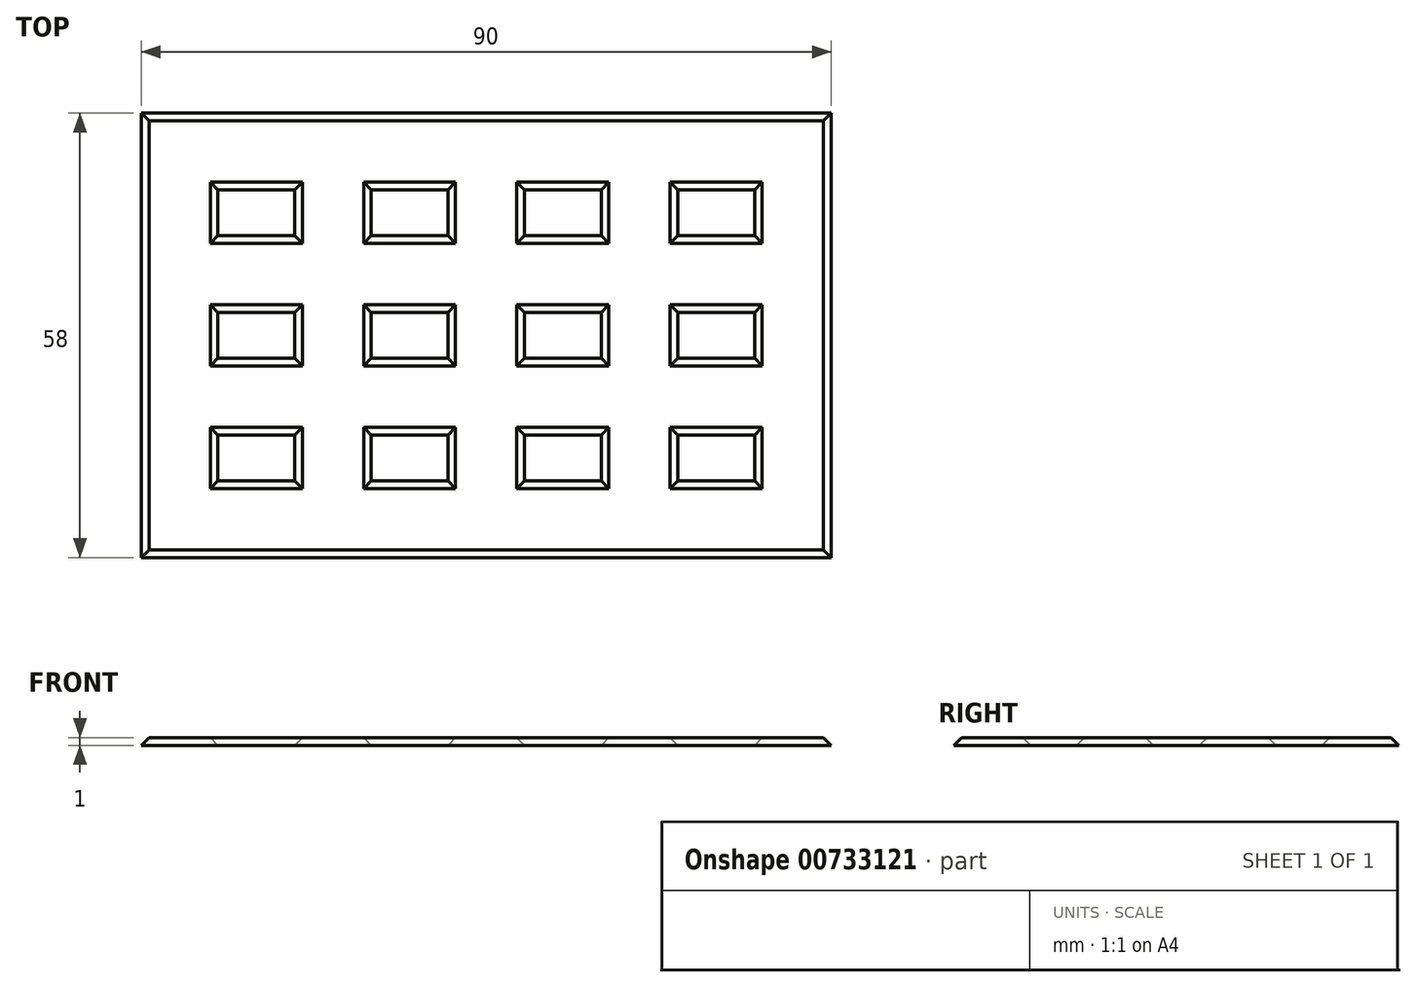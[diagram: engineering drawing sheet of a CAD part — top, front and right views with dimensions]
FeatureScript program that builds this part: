
annotation { "Feature Type Name" : "Feature", "Feature Type Description" : "" }
export const myFeature = defineFeature(function(context is Context, id is Id, definition is map)
    precondition{}
    {
        {
            var Q0;
            Q0=qCreatedBy(makeId("Top.planeOp"),FACE);
            var sketch = newSketch(context, id + "F0", { "sketchPlane" : qUnion([Q0])});
            skPoint(sketch, "E0.middle", {"position": v(0, 0) * mm});
            skLineSegment(sketch, "E1.bottom", {"start": v(-40, 15) * mm, "end": v(-30, 15) * mm});
            skLineSegment(sketch, "E1.top", {"start": v(-40, 9) * mm, "end": v(-30, 9) * mm});
            skLineSegment(sketch, "E1.left", {"start": v(-40, 15) * mm, "end": v(-40, 9) * mm});
            skLineSegment(sketch, "E1.right", {"start": v(-30, 15) * mm, "end": v(-30, 9) * mm});
            skLineSegment(sketch, "E2.bottom", {"start": v(-40, 9) * mm, "end": v(-30, 9) * mm, "construction": true});
            skLineSegment(sketch, "E2.top", {"start": v(-40, -1) * mm, "end": v(-30, -1) * mm, "construction": true});
            skLineSegment(sketch, "E2.left", {"start": v(-40, 9) * mm, "end": v(-40, -1) * mm, "construction": true});
            skLineSegment(sketch, "E2.right", {"start": v(-30, 9) * mm, "end": v(-30, -1) * mm, "construction": true});
            skLineSegment(sketch, "E3.bottom", {"start": v(-40, -1) * mm, "end": v(-30, -1) * mm});
            skLineSegment(sketch, "E3.top", {"start": v(-40, -7) * mm, "end": v(-30, -7) * mm});
            skLineSegment(sketch, "E3.left", {"start": v(-40, -1) * mm, "end": v(-40, -7) * mm});
            skLineSegment(sketch, "E3.right", {"start": v(-30, -1) * mm, "end": v(-30, -7) * mm});
            skLineSegment(sketch, "E4.bottom", {"start": v(-40, -7) * mm, "end": v(-30, -7) * mm, "construction": true});
            skLineSegment(sketch, "E4.top", {"start": v(-40, -17) * mm, "end": v(-30, -17) * mm, "construction": true});
            skLineSegment(sketch, "E4.left", {"start": v(-40, -7) * mm, "end": v(-40, -17) * mm, "construction": true});
            skLineSegment(sketch, "E4.right", {"start": v(-30, -7) * mm, "end": v(-30, -17) * mm, "construction": true});
            skLineSegment(sketch, "E5.bottom", {"start": v(-40, -17) * mm, "end": v(-30, -17) * mm});
            skLineSegment(sketch, "E5.top", {"start": v(-40, -23) * mm, "end": v(-30, -23) * mm});
            skLineSegment(sketch, "E5.left", {"start": v(-40, -17) * mm, "end": v(-40, -23) * mm});
            skLineSegment(sketch, "E5.right", {"start": v(-30, -17) * mm, "end": v(-30, -23) * mm});
            skLineSegment(sketch, "E6.bottom", {"start": v(-40, -23) * mm, "end": v(-30, -23) * mm, "construction": true});
            skLineSegment(sketch, "E6.top", {"start": v(-40, -33) * mm, "end": v(-30, -33) * mm, "construction": true});
            skLineSegment(sketch, "E6.left", {"start": v(-40, -23) * mm, "end": v(-40, -33) * mm, "construction": true});
            skLineSegment(sketch, "E6.right", {"start": v(-30, -23) * mm, "end": v(-30, -33) * mm, "construction": true});
            skLineSegment(sketch, "E7.bottom", {"start": v(-50, 25) * mm, "end": v(40, 25) * mm});
            skLineSegment(sketch, "E7.top", {"start": v(-50, -33) * mm, "end": v(40, -33) * mm});
            skLineSegment(sketch, "E7.left", {"start": v(-50, 25) * mm, "end": v(-50, -33) * mm});
            skLineSegment(sketch, "E7.right", {"start": v(40, 25) * mm, "end": v(40, -33) * mm});
            skLineSegment(sketch, "E8.bottom", {"start": v(-30, 15) * mm, "end": v(-20, 15) * mm, "construction": true});
            skLineSegment(sketch, "E8.top", {"start": v(-30, 9) * mm, "end": v(-20, 9) * mm, "construction": true});
            skLineSegment(sketch, "E8.left", {"start": v(-30, 15) * mm, "end": v(-30, 9) * mm, "construction": true});
            skLineSegment(sketch, "E8.right", {"start": v(-20, 15) * mm, "end": v(-20, 9) * mm, "construction": true});
            skLineSegment(sketch, "E9.bottom", {"start": v(-20, 9) * mm, "end": v(-30, 9) * mm, "construction": true});
            skLineSegment(sketch, "E9.top", {"start": v(-20, -1) * mm, "end": v(-30, -1) * mm, "construction": true});
            skLineSegment(sketch, "E9.left", {"start": v(-20, 9) * mm, "end": v(-20, -1) * mm, "construction": true});
            skLineSegment(sketch, "E10.top", {"start": v(-20, -7) * mm, "end": v(-30, -7) * mm, "construction": true});
            skLineSegment(sketch, "E10.left", {"start": v(-20, -1) * mm, "end": v(-20, -7) * mm, "construction": true});
            skLineSegment(sketch, "E10.right", {"start": v(-30, -1) * mm, "end": v(-30, -7) * mm, "construction": true});
            skLineSegment(sketch, "E11.top", {"start": v(-20, -17) * mm, "end": v(-30, -17) * mm, "construction": true});
            skLineSegment(sketch, "E11.left", {"start": v(-20, -7) * mm, "end": v(-20, -17) * mm, "construction": true});
            skLineSegment(sketch, "E12.top", {"start": v(-20, -23) * mm, "end": v(-30, -23) * mm, "construction": true});
            skLineSegment(sketch, "E12.left", {"start": v(-20, -17) * mm, "end": v(-20, -23) * mm, "construction": true});
            skLineSegment(sketch, "E12.right", {"start": v(-30, -17) * mm, "end": v(-30, -23) * mm, "construction": true});
            skLineSegment(sketch, "E13.bottom", {"start": v(-20, 15) * mm, "end": v(-10, 15) * mm});
            skLineSegment(sketch, "E13.top", {"start": v(-20, 9) * mm, "end": v(-10, 9) * mm});
            skLineSegment(sketch, "E13.left", {"start": v(-20, 15) * mm, "end": v(-20, 9) * mm});
            skLineSegment(sketch, "E13.right", {"start": v(-10, 15) * mm, "end": v(-10, 9) * mm});
            skLineSegment(sketch, "E14.bottom", {"start": v(-20, -1) * mm, "end": v(-10, -1) * mm});
            skLineSegment(sketch, "E14.top", {"start": v(-20, -7) * mm, "end": v(-10, -7) * mm});
            skLineSegment(sketch, "E14.left", {"start": v(-20, -1) * mm, "end": v(-20, -7) * mm});
            skLineSegment(sketch, "E14.right", {"start": v(-10, -1) * mm, "end": v(-10, -7) * mm});
            skLineSegment(sketch, "E15.bottom", {"start": v(-20, -17) * mm, "end": v(-10, -17) * mm});
            skLineSegment(sketch, "E15.top", {"start": v(-20, -23) * mm, "end": v(-10, -23) * mm});
            skLineSegment(sketch, "E15.left", {"start": v(-20, -17) * mm, "end": v(-20, -23) * mm});
            skLineSegment(sketch, "E15.right", {"start": v(-10, -17) * mm, "end": v(-10, -23) * mm});
            skLineSegment(sketch, "E16.bottom", {"start": v(-10, 15) * mm, "end": v(0, 15) * mm, "construction": true});
            skLineSegment(sketch, "E16.top", {"start": v(-10, 9) * mm, "end": v(0, 9) * mm, "construction": true});
            skLineSegment(sketch, "E16.left", {"start": v(-10, 15) * mm, "end": v(-10, 9) * mm, "construction": true});
            skLineSegment(sketch, "E16.right", {"start": v(0, 15) * mm, "end": v(0, 9) * mm, "construction": true});
            skLineSegment(sketch, "E17.bottom", {"start": v(-10, -1) * mm, "end": v(0, -1) * mm, "construction": true});
            skLineSegment(sketch, "E17.top", {"start": v(-10, -7) * mm, "end": v(0, -7) * mm, "construction": true});
            skLineSegment(sketch, "E17.left", {"start": v(-10, -1) * mm, "end": v(-10, -7) * mm, "construction": true});
            skLineSegment(sketch, "E17.right", {"start": v(0, -1) * mm, "end": v(0, -7) * mm, "construction": true});
            skLineSegment(sketch, "E18.bottom", {"start": v(-10, -17) * mm, "end": v(0, -17) * mm, "construction": true});
            skLineSegment(sketch, "E18.top", {"start": v(-10, -23) * mm, "end": v(0, -23) * mm, "construction": true});
            skLineSegment(sketch, "E18.left", {"start": v(-10, -17) * mm, "end": v(-10, -23) * mm, "construction": true});
            skLineSegment(sketch, "E18.right", {"start": v(0, -17) * mm, "end": v(0, -23) * mm, "construction": true});
            skLineSegment(sketch, "E19.bottom", {"start": v(0, 15) * mm, "end": v(10, 15) * mm});
            skLineSegment(sketch, "E19.top", {"start": v(0, 9) * mm, "end": v(10, 9) * mm});
            skLineSegment(sketch, "E19.left", {"start": v(0, 15) * mm, "end": v(0, 9) * mm});
            skLineSegment(sketch, "E19.right", {"start": v(10, 15) * mm, "end": v(10, 9) * mm});
            skLineSegment(sketch, "E20.bottom", {"start": v(0, -7) * mm, "end": v(10, -7) * mm});
            skLineSegment(sketch, "E20.top", {"start": v(0, -1) * mm, "end": v(10, -1) * mm});
            skLineSegment(sketch, "E20.left", {"start": v(0, -7) * mm, "end": v(0, -1) * mm});
            skLineSegment(sketch, "E20.right", {"start": v(10, -7) * mm, "end": v(10, -1) * mm});
            skLineSegment(sketch, "E21.bottom", {"start": v(0, -23) * mm, "end": v(10, -23) * mm});
            skLineSegment(sketch, "E21.top", {"start": v(0, -17) * mm, "end": v(10, -17) * mm});
            skLineSegment(sketch, "E21.left", {"start": v(0, -23) * mm, "end": v(0, -17) * mm});
            skLineSegment(sketch, "E21.right", {"start": v(10, -23) * mm, "end": v(10, -17) * mm});
            skLineSegment(sketch, "E22.bottom", {"start": v(10, 9) * mm, "end": v(20, 9) * mm, "construction": true});
            skLineSegment(sketch, "E22.top", {"start": v(10, 15) * mm, "end": v(20, 15) * mm, "construction": true});
            skLineSegment(sketch, "E22.left", {"start": v(10, 9) * mm, "end": v(10, 15) * mm, "construction": true});
            skLineSegment(sketch, "E22.right", {"start": v(20, 9) * mm, "end": v(20, 15) * mm, "construction": true});
            skLineSegment(sketch, "E23.bottom", {"start": v(10, -7) * mm, "end": v(20, -7) * mm, "construction": true});
            skLineSegment(sketch, "E23.top", {"start": v(10, -1) * mm, "end": v(20, -1) * mm, "construction": true});
            skLineSegment(sketch, "E23.left", {"start": v(10, -7) * mm, "end": v(10, -1) * mm, "construction": true});
            skLineSegment(sketch, "E23.right", {"start": v(20, -7) * mm, "end": v(20, -1) * mm, "construction": true});
            skLineSegment(sketch, "E24.bottom", {"start": v(10, -23) * mm, "end": v(20, -23) * mm, "construction": true});
            skLineSegment(sketch, "E24.top", {"start": v(10, -17) * mm, "end": v(20, -17) * mm, "construction": true});
            skLineSegment(sketch, "E24.left", {"start": v(10, -23) * mm, "end": v(10, -17) * mm, "construction": true});
            skLineSegment(sketch, "E24.right", {"start": v(20, -23) * mm, "end": v(20, -17) * mm, "construction": true});
            skLineSegment(sketch, "E25.bottom", {"start": v(20, -23) * mm, "end": v(30, -23) * mm});
            skLineSegment(sketch, "E25.top", {"start": v(20, -17) * mm, "end": v(30, -17) * mm});
            skLineSegment(sketch, "E25.left", {"start": v(20, -23) * mm, "end": v(20, -17) * mm});
            skLineSegment(sketch, "E25.right", {"start": v(30, -23) * mm, "end": v(30, -17) * mm});
            skLineSegment(sketch, "E26.bottom", {"start": v(20, -7) * mm, "end": v(30, -7) * mm});
            skLineSegment(sketch, "E26.top", {"start": v(20, -1) * mm, "end": v(30, -1) * mm});
            skLineSegment(sketch, "E26.left", {"start": v(20, -7) * mm, "end": v(20, -1) * mm});
            skLineSegment(sketch, "E26.right", {"start": v(30, -7) * mm, "end": v(30, -1) * mm});
            skLineSegment(sketch, "E27.bottom", {"start": v(20, 9) * mm, "end": v(30, 9) * mm});
            skLineSegment(sketch, "E27.top", {"start": v(20, 15) * mm, "end": v(30, 15) * mm});
            skLineSegment(sketch, "E27.left", {"start": v(20, 9) * mm, "end": v(20, 15) * mm});
            skLineSegment(sketch, "E27.right", {"start": v(30, 9) * mm, "end": v(30, 15) * mm});
            skSolve(sketch);
        }
        {
            var Q0;
            Q0 = qSketchRegion(id + "F0", true);
            extrude(context, id + "F1", {"entities" : qUnion([Q0]), "depth" : 1 * mm, "offsetDistance" : 25 * mm});
        }
        {
            var Q0;
            Q0=makeQuery(id+"F1.opExtrude","CAP_EDGE",EDGE,{"disambiguationData":[OSD([sQuery(id+"F0.wireOp",EDGE,"E1.bottom")])],"isStart":false});
            var Q1;
            Q1=makeQuery(id+"F1.opExtrude","CAP_EDGE",EDGE,{"disambiguationData":[OSD([sQuery(id+"F0.wireOp",EDGE,"E1.left")])],"isStart":false});
            var Q2;
            Q2=makeQuery(id+"F1.opExtrude","CAP_EDGE",EDGE,{"disambiguationData":[OSD([sQuery(id+"F0.wireOp",EDGE,"E1.top")])],"isStart":false});
            var Q3;
            Q3=makeQuery(id+"F1.opExtrude","CAP_EDGE",EDGE,{"disambiguationData":[OSD([sQuery(id+"F0.wireOp",EDGE,"E1.right")])],"isStart":false});
            var Q4;
            Q4=makeQuery(id+"F1.opExtrude","CAP_EDGE",EDGE,{"disambiguationData":[OSD([sQuery(id+"F0.wireOp",EDGE,"E3.right")])],"isStart":false});
            var Q5;
            Q5=makeQuery(id+"F1.opExtrude","CAP_EDGE",EDGE,{"disambiguationData":[OSD([sQuery(id+"F0.wireOp",EDGE,"E3.top")])],"isStart":false});
            var Q6;
            Q6=makeQuery(id+"F1.opExtrude","CAP_EDGE",EDGE,{"disambiguationData":[OSD([sQuery(id+"F0.wireOp",EDGE,"E3.bottom")])],"isStart":false});
            var Q7;
            Q7=makeQuery(id+"F1.opExtrude","CAP_EDGE",EDGE,{"disambiguationData":[OSD([sQuery(id+"F0.wireOp",EDGE,"E3.left")])],"isStart":false});
            var Q8;
            Q8=makeQuery(id+"F1.opExtrude","CAP_EDGE",EDGE,{"disambiguationData":[OSD([sQuery(id+"F0.wireOp",EDGE,"E5.bottom")])],"isStart":false});
            var Q9;
            Q9=makeQuery(id+"F1.opExtrude","CAP_EDGE",EDGE,{"disambiguationData":[OSD([sQuery(id+"F0.wireOp",EDGE,"E5.left")])],"isStart":false});
            var Q10;
            Q10=makeQuery(id+"F1.opExtrude","CAP_EDGE",EDGE,{"disambiguationData":[OSD([sQuery(id+"F0.wireOp",EDGE,"E5.top")])],"isStart":false});
            var Q11;
            Q11=makeQuery(id+"F1.opExtrude","CAP_EDGE",EDGE,{"disambiguationData":[OSD([sQuery(id+"F0.wireOp",EDGE,"E5.right")])],"isStart":false});
            var Q12;
            Q12=makeQuery(id+"F1.opExtrude","CAP_FACE",FACE,{"disambiguationData":[OSD([sQuery(id+"F0.wireOp",EDGE,"E1.bottom"),sQuery(id+"F0.wireOp",EDGE,"E1.top"),sQuery(id+"F0.wireOp",EDGE,"E1.left"),sQuery(id+"F0.wireOp",EDGE,"E1.right"),sQuery(id+"F0.wireOp",EDGE,"E3.bottom"),sQuery(id+"F0.wireOp",EDGE,"E3.top"),sQuery(id+"F0.wireOp",EDGE,"E3.left"),sQuery(id+"F0.wireOp",EDGE,"E3.right"),sQuery(id+"F0.wireOp",EDGE,"E5.bottom"),sQuery(id+"F0.wireOp",EDGE,"E5.top"),sQuery(id+"F0.wireOp",EDGE,"E5.left"),sQuery(id+"F0.wireOp",EDGE,"E5.right"),sQuery(id+"F0.wireOp",EDGE,"E7.bottom"),sQuery(id+"F0.wireOp",EDGE,"E7.top"),sQuery(id+"F0.wireOp",EDGE,"E7.left"),sQuery(id+"F0.wireOp",EDGE,"E7.right")])],"isStart":false});
            chamfer(context, id + "F2", {"entities" : qUnion([Q0, Q1, Q2, Q3, Q4, Q5, Q6, Q7, Q8, Q9, Q10, Q11, Q12]), "width" : 1 * mm, "tangentPropagation" : true});
        }
    });
